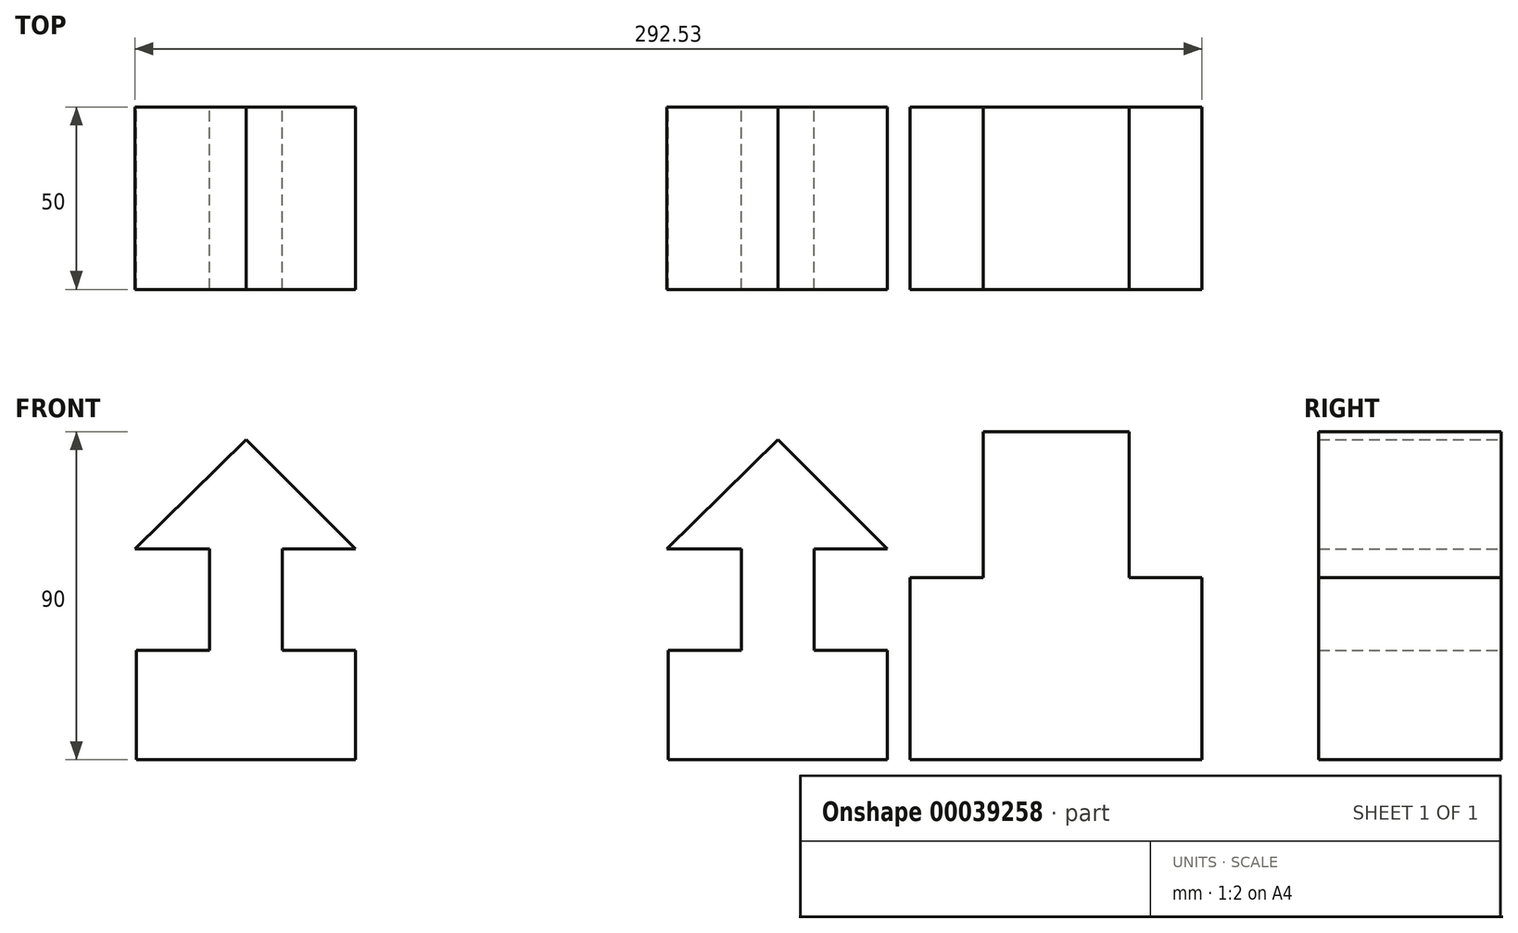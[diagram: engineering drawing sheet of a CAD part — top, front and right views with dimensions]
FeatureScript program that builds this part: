
annotation { "Feature Type Name" : "Feature", "Feature Type Description" : "" }
export const myFeature = defineFeature(function(context is Context, id is Id, definition is map)
    precondition{}
    {
        {
            var Q0;
            Q0=qCreatedBy(makeId("Front.planeOp"),FACE);
            var sketch = newSketch(context, id + "F0", { "sketchPlane" : qUnion([Q0])});
            skLineSegment(sketch, "E0.bottom", {"start": v(-60, 30) * mm, "end": v(0, 30) * mm});
            skLineSegment(sketch, "E0.top", {"start": v(-60, 0) * mm, "end": v(0, 0) * mm});
            skLineSegment(sketch, "E0.left", {"start": v(-60, 30) * mm, "end": v(-60, 0) * mm});
            skLineSegment(sketch, "E0.right", {"start": v(0, 30) * mm, "end": v(0, 0) * mm});
            skLineSegment(sketch, "E1.bottom", {"start": v(-40, 30) * mm, "end": v(-20, 30) * mm});
            skLineSegment(sketch, "E1.top", {"start": v(-40, 57.77) * mm, "end": v(-20, 57.77) * mm});
            skLineSegment(sketch, "E1.left", {"start": v(-40, 30) * mm, "end": v(-40, 57.77) * mm});
            skLineSegment(sketch, "E1.right", {"start": v(-20, 30) * mm, "end": v(-20, 57.77) * mm});
            skLineSegment(sketch, "E2", {"start": v(-40, 57.77) * mm, "end": v(-60.49, 57.77) * mm});
            skLineSegment(sketch, "E3", {"start": v(-20, 57.77) * mm, "end": v(0, 57.77) * mm});
            skLineSegment(sketch, "E4", {"start": v(-30, 57.77) * mm, "end": v(-30, 87.77) * mm});
            skLineSegment(sketch, "E5", {"start": v(-30, 87.77) * mm, "end": v(-60.49, 57.77) * mm});
            skLineSegment(sketch, "E6", {"start": v(-30, 87.77) * mm, "end": v(0, 57.77) * mm});
            skSolve(sketch);
        }
        {
            var Q0;
            Q0 = qSketchRegion(id + "F0", true);
            extrude(context, id + "F1", {"entities" : qUnion([Q0]), "depth" : 50 * mm});
        }
        {
            var Q0;
            Q0=qCreatedBy(makeId("Front.planeOp"),FACE);
            var sketch = newSketch(context, id + "F2", { "sketchPlane" : qUnion([Q0])});
            skLineSegment(sketch, "E7.bottom", {"start": v(6.25, 50) * mm, "end": v(86.25, 50) * mm});
            skLineSegment(sketch, "E7.top", {"start": v(6.25, 0) * mm, "end": v(86.25, 0) * mm});
            skLineSegment(sketch, "E7.left", {"start": v(6.25, 50) * mm, "end": v(6.25, 0) * mm});
            skLineSegment(sketch, "E7.right", {"start": v(86.25, 50) * mm, "end": v(86.25, 0) * mm});
            skLineSegment(sketch, "E8.bottom", {"start": v(26.25, 90) * mm, "end": v(66.25, 90) * mm});
            skLineSegment(sketch, "E8.top", {"start": v(26.25, 50) * mm, "end": v(66.25, 50) * mm});
            skLineSegment(sketch, "E8.left", {"start": v(26.25, 90) * mm, "end": v(26.25, 50) * mm});
            skLineSegment(sketch, "E8.right", {"start": v(66.25, 90) * mm, "end": v(66.25, 50) * mm});
            skSolve(sketch);
        }
        {
            var Q0;
            Q0=makeQuery(id+"F2.imprint","IMPRINT",FACE,{"disambiguationData":[TD([[makeQuery(id+"F2.imprint","IMPRINT",EDGE,{"derivedFrom":sQuery(id+"F2.wireOp",EDGE,"E7.top")}),1.0]])]});
            var Q1;
            Q1=makeQuery(id+"F2.imprint","IMPRINT",FACE,{"disambiguationData":[TD([[makeQuery(id+"F2.imprint","IMPRINT",EDGE,{"derivedFrom":sQuery(id+"F2.wireOp",EDGE,"E8.bottom")}),-1.0]])]});
            extrude(context, id + "F3", {"entities" : qUnion([Q0, Q1]), "depth" : 50 * mm});
        }
        {
            var Q0;
            Q0=makeQuery(id+"F1.opExtrude","SWEPT_BODY",BODY,{"disambiguationData":[OSD([sQuery(id+"F0.wireOp",EDGE,"E0.bottom"),sQuery(id+"F0.wireOp",EDGE,"E0.top"),sQuery(id+"F0.wireOp",EDGE,"E0.left"),sQuery(id+"F0.wireOp",EDGE,"E0.right"),sQuery(id+"F0.wireOp",EDGE,"E1.left"),sQuery(id+"F0.wireOp",EDGE,"E1.right"),sQuery(id+"F0.wireOp",EDGE,"E2"),sQuery(id+"F0.wireOp",EDGE,"E3"),sQuery(id+"F0.wireOp",EDGE,"E5"),sQuery(id+"F0.wireOp",EDGE,"E6")])]});
            transform(context, id + "F4", {"entities" : qUnion([Q0]), "transformType" : TransformType.TRANSLATION_3D, "dx" : -145.8 * mm, "dy" : 0 * mm, "dz" : 0 * mm, "makeCopy" : true});
        }
    });
